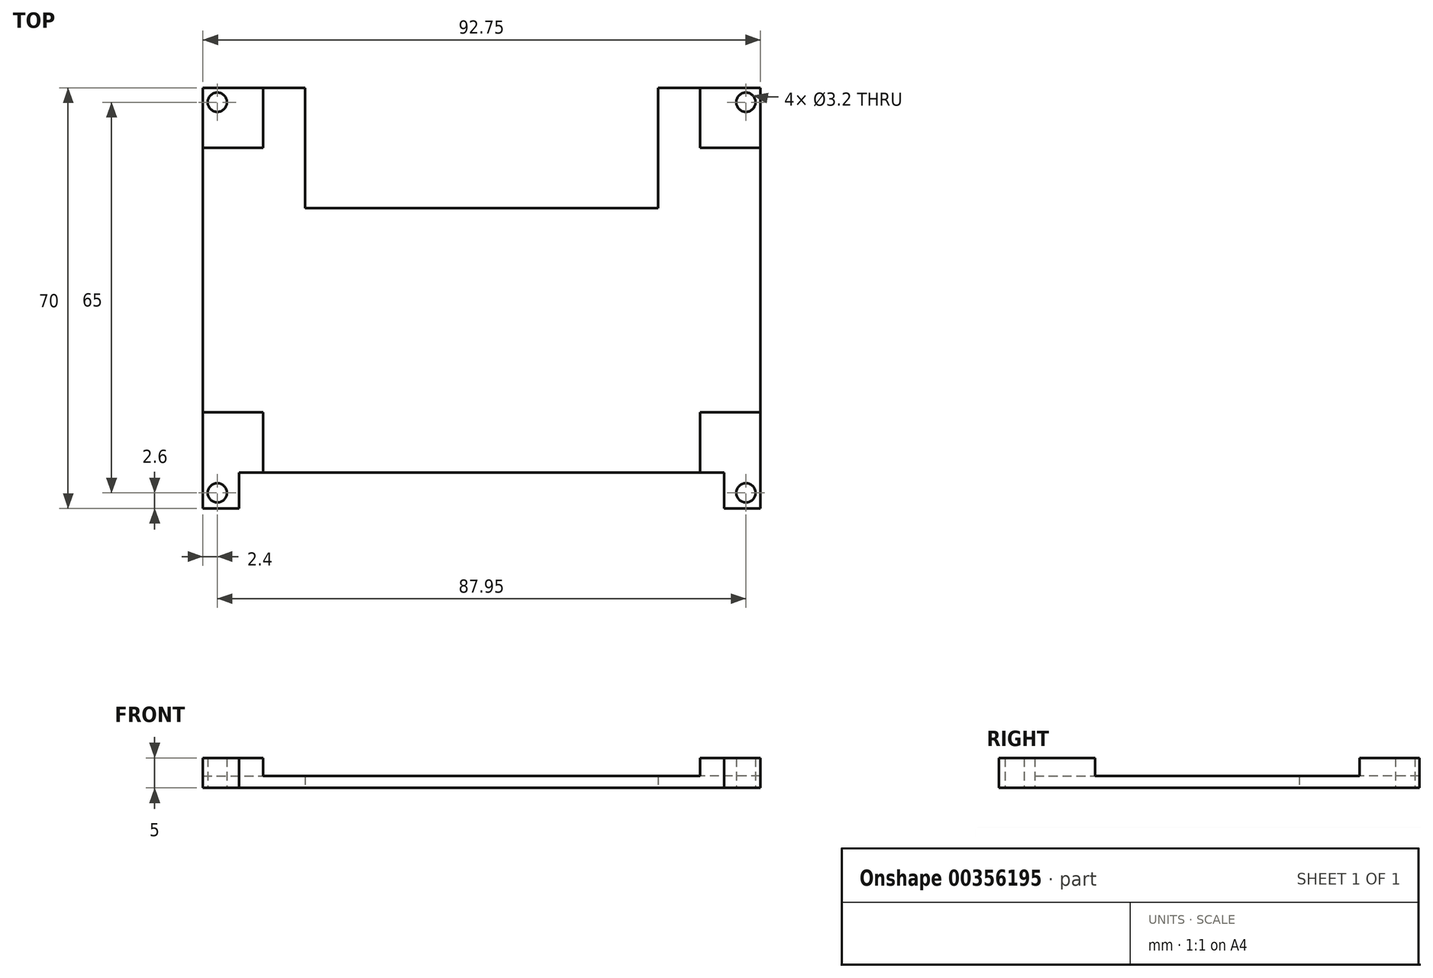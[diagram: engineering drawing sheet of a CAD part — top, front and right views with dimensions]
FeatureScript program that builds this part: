
annotation { "Feature Type Name" : "Feature", "Feature Type Description" : "" }
export const myFeature = defineFeature(function(context is Context, id is Id, definition is map)
    precondition{}
    {
        {
            var Q0;
            Q0=qCreatedBy(makeId("Top.planeOp"),FACE);
            var sketch = newSketch(context, id + "F0", { "sketchPlane" : qUnion([Q0])});
            skLineSegment(sketch, "E0", {"start": v(-27.94, 20) * mm, "end": v(-27.94, 0) * mm});
            skLineSegment(sketch, "E1", {"start": v(-27.94, 0) * mm, "end": v(30.81, 0) * mm});
            skLineSegment(sketch, "E2", {"start": v(30.81, 0) * mm, "end": v(30.81, 20) * mm});
            skLineSegment(sketch, "E3", {"start": v(30.81, 20) * mm, "end": v(47.81, 20) * mm});
            skLineSegment(sketch, "E4", {"start": v(47.81, 20) * mm, "end": v(47.81, -44) * mm});
            skLineSegment(sketch, "E5", {"start": v(47.81, -44) * mm, "end": v(-44.94, -44) * mm});
            skLineSegment(sketch, "E6", {"start": v(-44.94, -44) * mm, "end": v(-44.94, 20) * mm});
            skLineSegment(sketch, "E7", {"start": v(-44.94, 20) * mm, "end": v(-27.94, 20) * mm});
            skCircle(sketch, "E8", {"center": v(-42.54, 17.6) * mm, "radius": 1.6 * mm});
            skCircle(sketch, "E9", {"center": v(45.41, 17.6) * mm, "radius": 1.6 * mm});
            skSolve(sketch);
        }
        {
            var Q0;
            Q0 = qSketchRegion(id + "F0", true);
            extrude(context, id + "F1", {"entities" : qUnion([Q0]), "depth" : 2 * mm});
        }
        {
            var Q0;
            Q0=makeQuery(id+"F1.opExtrude","CAP_FACE",FACE,{"disambiguationData":[OSD([sQuery(id+"F0.wireOp",EDGE,"E0"),sQuery(id+"F0.wireOp",EDGE,"E1"),sQuery(id+"F0.wireOp",EDGE,"E2"),sQuery(id+"F0.wireOp",EDGE,"E3"),sQuery(id+"F0.wireOp",EDGE,"E4"),sQuery(id+"F0.wireOp",EDGE,"E5"),sQuery(id+"F0.wireOp",EDGE,"E6"),sQuery(id+"F0.wireOp",EDGE,"E7"),sQuery(id+"F0.wireOp",EDGE,"E8"),sQuery(id+"F0.wireOp",EDGE,"E9")])],"isStart":false});
            var sketch = newSketch(context, id + "F2", { "sketchPlane" : qUnion([Q0])});
            skCircle(sketch, "E10", {"center": v(-42.54, 17.6) * mm, "radius": 1.6 * mm});
            skCircle(sketch, "E11", {"center": v(45.41, 17.6) * mm, "radius": 1.6 * mm});
            skLineSegment(sketch, "E12.bottom", {"start": v(-44.94, 20) * mm, "end": v(-34.94, 20) * mm});
            skLineSegment(sketch, "E12.top", {"start": v(-44.94, 10) * mm, "end": v(-34.94, 10) * mm});
            skLineSegment(sketch, "E12.left", {"start": v(-44.94, 20) * mm, "end": v(-44.94, 10) * mm});
            skLineSegment(sketch, "E12.right", {"start": v(-34.94, 20) * mm, "end": v(-34.94, 10) * mm});
            skLineSegment(sketch, "E13.bottom", {"start": v(47.81, 20) * mm, "end": v(37.81, 20) * mm});
            skLineSegment(sketch, "E13.top", {"start": v(47.81, 10) * mm, "end": v(37.81, 10) * mm});
            skLineSegment(sketch, "E13.left", {"start": v(47.81, 20) * mm, "end": v(47.81, 10) * mm});
            skLineSegment(sketch, "E13.right", {"start": v(37.81, 20) * mm, "end": v(37.81, 10) * mm});
            skLineSegment(sketch, "E14.bottom", {"start": v(-44.94, -44) * mm, "end": v(-34.94, -44) * mm});
            skLineSegment(sketch, "E14.top", {"start": v(-44.94, -34) * mm, "end": v(-34.94, -34) * mm});
            skLineSegment(sketch, "E14.left", {"start": v(-44.94, -44) * mm, "end": v(-44.94, -34) * mm});
            skLineSegment(sketch, "E14.right", {"start": v(-34.94, -44) * mm, "end": v(-34.94, -34) * mm});
            skLineSegment(sketch, "E15.bottom", {"start": v(47.81, -44) * mm, "end": v(37.81, -44) * mm});
            skLineSegment(sketch, "E15.top", {"start": v(47.81, -34) * mm, "end": v(37.81, -34) * mm});
            skLineSegment(sketch, "E15.left", {"start": v(47.81, -44) * mm, "end": v(47.81, -34) * mm});
            skLineSegment(sketch, "E15.right", {"start": v(37.81, -44) * mm, "end": v(37.81, -34) * mm});
            skSolve(sketch);
        }
        {
            var Q0;
            Q0 = qSketchRegion(id + "F2", true);
            extrude(context, id + "F3", {"entities" : qUnion([Q0]), "operationType" : NewBodyOperationType.ADD, "depth" : 3 * mm});
        }
        {
            var Q0;
            Q0=makeQuery(id+"F1.opExtrude","CAP_FACE",FACE,{"disambiguationData":[OSD([sQuery(id+"F0.wireOp",EDGE,"E0"),sQuery(id+"F0.wireOp",EDGE,"E1"),sQuery(id+"F0.wireOp",EDGE,"E2"),sQuery(id+"F0.wireOp",EDGE,"E3"),sQuery(id+"F0.wireOp",EDGE,"E4"),sQuery(id+"F0.wireOp",EDGE,"E5"),sQuery(id+"F0.wireOp",EDGE,"E6"),sQuery(id+"F0.wireOp",EDGE,"E7"),sQuery(id+"F0.wireOp",EDGE,"E8"),sQuery(id+"F0.wireOp",EDGE,"E9")])],"isStart":true});
            var sketch = newSketch(context, id + "F4", { "sketchPlane" : qUnion([Q0])});
            skLineSegment(sketch, "E16.bottom", {"start": v(-44.94, 44) * mm, "end": v(-38.94, 44) * mm});
            skLineSegment(sketch, "E16.top", {"start": v(-44.94, 50) * mm, "end": v(-38.94, 50) * mm});
            skLineSegment(sketch, "E16.left", {"start": v(-44.94, 44) * mm, "end": v(-44.94, 50) * mm});
            skLineSegment(sketch, "E16.right", {"start": v(-38.94, 44) * mm, "end": v(-38.94, 50) * mm});
            skLineSegment(sketch, "E17.bottom", {"start": v(47.81, 44) * mm, "end": v(41.81, 44) * mm});
            skLineSegment(sketch, "E17.top", {"start": v(47.81, 50) * mm, "end": v(41.81, 50) * mm});
            skLineSegment(sketch, "E17.left", {"start": v(47.81, 44) * mm, "end": v(47.81, 50) * mm});
            skLineSegment(sketch, "E17.right", {"start": v(41.81, 44) * mm, "end": v(41.81, 50) * mm});
            skCircle(sketch, "E18", {"center": v(-42.54, 47.4) * mm, "radius": 1.6 * mm});
            skCircle(sketch, "E19", {"center": v(45.41, 47.4) * mm, "radius": 1.6 * mm});
            skSolve(sketch);
        }
        {
            var Q0;
            Q0 = qSketchRegion(id + "F4", true);
            extrude(context, id + "F5", {"entities" : qUnion([Q0]), "operationType" : NewBodyOperationType.ADD, "oppositeDirection" : true, "depth" : 5 * mm});
        }
    });
